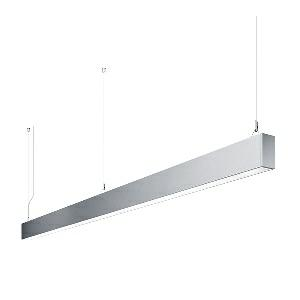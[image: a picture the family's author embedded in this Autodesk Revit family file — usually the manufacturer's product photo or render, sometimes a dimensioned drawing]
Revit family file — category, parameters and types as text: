
# Revit family: dotoo_line_-_dlp_3000_840_d_00805829_f52e
name_source: partatom
category: Lighting Fixtures
units: mm (PartAtom-declared; Revit-internal decimal feet)

## family parameters
Cut with Voids When Loaded = No
Host = Face
Light Source = No
Part Type = Normal
Room Calculation Point = No
Round Connector Dimension = Use Diameter
Shared = No

## types (1)
- DOTOO.line - DLP 3000/840/D (1 x LED, 2750 lm, 4000K)
    Apparent Load = 26 VA
    Approval mark = CE
    CIE Flux Codes = 67 91 98 100 100
    Color Rendering = 80-89
    Color Temperature = 4000K
    Control Gear = Electronic ballast
    Default Elevation = 1800 mm
    Description = DLP 3000/840/D|Suspended luminaire|light source: LED|connected load: 220-240 V, 50/60 Hz|Power consumption: approx. 26 W|standby: approx. 0,15|luminous flux: 2750 lm|luminous efficacy: 105 lm/W|light distribution: Direct|direct ratio: approx. 100 %|colour temperature: Cold white, ca. 4000 K|color rendering index (CRI): >= 80|chromaticity tolerance:  3 SDCM|System of protection: IP 40|technology: Continuously dimmable|luminaire body|material: Sectional aluminium|colour: Silver|lamp cover: Acrylic (PMMA), Clear|mains lead: 2.00 m With free stranded wires|Fastening: Steel cable 0.3 - 0.7 m|glare control: Prism aperture|luminance(L65): <= 3000 cd/m|unified glare rating(4H 8H): <=  19|special features: DALI Load 1x, TouchDIM - dimming via standard switch, Flicker-free, Suitable as emergency lighting|
    Frequency = 50 Hz
    Height = 110 mm
    Lamp = 1 x LED
    Lamp Light Flux = 2750 lm
    Lamp count = 1
    Length = 2256 mm
    Luminous efficacy = 106 lm/W
    Manufacturer = Waldmann
    ModVariant = No
    Model = 00805829
    Mounting Place = Ceiling
    Mounting Type = Pendant
    Number of Poles = 1
    OnlyDefault = Yes
    Power Factor = 1
    Product Name = DOTOO.line - DLP 3000/840/D
    Product group = Suspended luminaire
    ProductGroupID = 9
    Protection Class = Protection class I
    Protection Degree = IP 40
    RLX_Detail_Level = 1
    RLX_Emergency_Light_Flux = 0 lm
    RLX_Emergency_Type = 0
    RLX_Emergency_Type_DB = No
    RlxData = <blob elided: 23329 chars, md5=26f2febb>
    Socket = socket
    Standby Power = 0 W
    System Light Flux = 2750 lm
    System Power = 26 W
    Type Comments = Product without accessories
    Type Image = 113294000-00692533.jpg
    URL = http://relux.com
    VarID = ---
    Voltage = 230 V
    Voltage Range = 220-240 V
    Weight = 0.00 kg
    Width = 60 mm  [stored 0.19685 ft]

note: [stored X ft] marks values corroborated as IEEE doubles in the binary element streams (Revit-internal decimal feet)

## geometry (parser evidence)
native form markers: Blend x4, Sweep x12
no freeform markers — native parametric forms only
